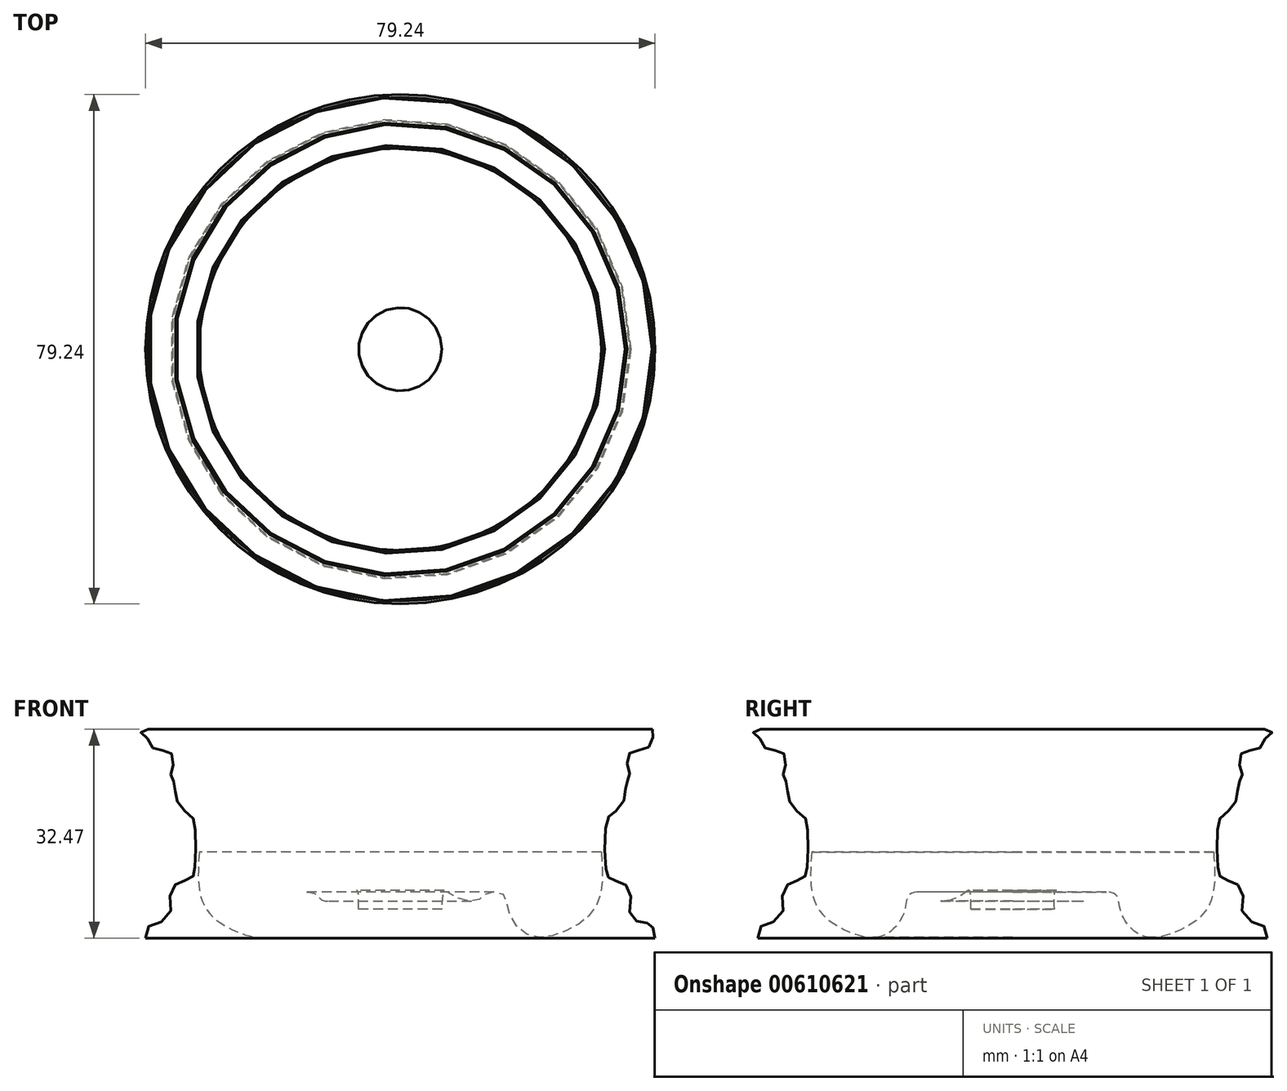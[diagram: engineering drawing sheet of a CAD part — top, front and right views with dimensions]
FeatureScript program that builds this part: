
annotation { "Feature Type Name" : "Feature", "Feature Type Description" : "" }
export const myFeature = defineFeature(function(context is Context, id is Id, definition is map)
    precondition{}
    {
        {
            var Q0;
            Q0=qCreatedBy(makeId("Right.planeOp"),FACE);
            var sketch = newSketch(context, id + "F0", { "sketchPlane" : qUnion([Q0])});
            skFitSpline(sketch, "E0", {"points": [v(-39.62, 17.84) * mm, v(-39.05, 19.79) * mm, v(-38.08, 20.19) * mm, v(-35.85, 21.19) * mm, v(-35.71, 25.32) * mm, v(-33.5, 26.77) * mm, v(-32.41, 27.23) * mm, v(-31.92, 28.97) * mm, v(-32.18, 36.33) * mm, v(-33.04, 37.18) * mm, v(-34.89, 39.57) * mm, v(-35.09, 41.85) * mm, v(-35.72, 42.86) * mm, v(-35.36, 44.5) * mm, v(-35.7, 46.69) * mm, v(-37.57, 47.12) * mm, v(-39.22, 48.34) * mm, v(-39.19, 50.3) * mm, v(-39.2, 50.3) * mm], "startDerivative": vector(0.09, 32.77) * mm, "endDerivative": vector(-4.77, 7.52) * mm});
            skLineSegment(sketch, "E1", {"start": v(0, 5.3) * mm, "end": v(0, 50.84) * mm});
            skLineSegment(sketch, "E2", {"start": v(-31.91, 36.04) * mm, "end": v(-31.91, 35.53) * mm});
            skSolve(sketch);
        }
        {
            var Q0;
            Q0=sQuery(id+"F0.wireOp",EDGE,"E0");
            var Q1;
            Q1=sQuery(id+"F0.wireOp",EDGE,"E1");
            revolve(context, id + "F1", {"bodyType" : ToolBodyType.SURFACE, "surfaceEntities" : qUnion([Q0]), "axis" : qUnion([Q1]), "revolveType" : RevolveType.FULL});
        }
        {
            var Q0;
            Q0=qCreatedBy(makeId("Right.planeOp"),FACE);
            var sketch = newSketch(context, id + "F2", { "sketchPlane" : qUnion([Q0])});
            skFitSpline(sketch, "E3", {"points": [v(31.27, 31.24) * mm, v(31.27, 25.37) * mm, v(29.49, 21.45) * mm, v(24.85, 18.6) * mm, v(20.04, 18.24) * mm, v(16.84, 21.98) * mm, v(15.95, 24.65) * mm, v(13.1, 24.65) * mm, v(12.2, 23.76) * mm, v(8.28, 24.3) * mm, v(6.68, 25.19) * mm, v(6.5, 22.51) * mm, v(6.5, 22.34) * mm], "startDerivative": vector(3.59, -53.72) * mm, "endDerivative": vector(-0.3, -4.34) * mm});
            skSolve(sketch);
        }
        {
            var Q0;
            Q0=sQuery(id+"F2.wireOp",EDGE,"E3");
            var Q1;
            Q1=sQuery(id+"F0.wireOp",EDGE,"E1");
            revolve(context, id + "F3", {"bodyType" : ToolBodyType.SURFACE, "surfaceEntities" : qUnion([Q0]), "axis" : qUnion([Q1]), "revolveType" : RevolveType.FULL});
        }
    });
